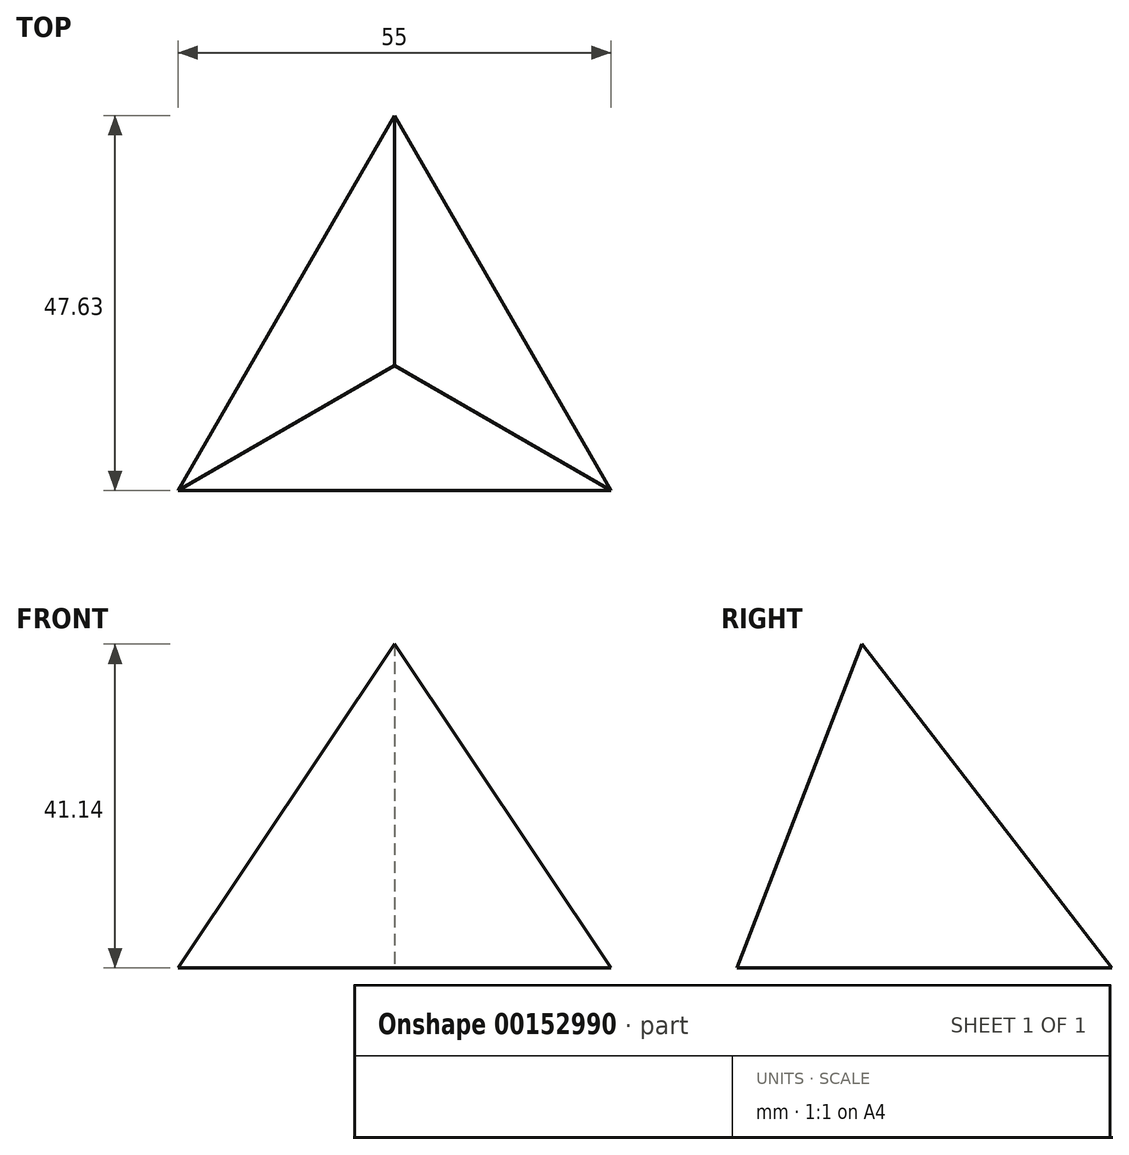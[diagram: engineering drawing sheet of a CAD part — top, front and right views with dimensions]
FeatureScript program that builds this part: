
annotation { "Feature Type Name" : "Feature", "Feature Type Description" : "" }
export const myFeature = defineFeature(function(context is Context, id is Id, definition is map)
    precondition{}
    {
        {
            var Q0;
            Q0=qCreatedBy(makeId("Top.planeOp"),FACE);
            var sketch = newSketch(context, id + "F0", { "sketchPlane" : qUnion([Q0])});
            skCircle(sketch, "E0.cCircle", {"center": v(0, 0) * mm, "radius": 31.75 * mm, "construction": true});
            skLineSegment(sketch, "E0.0", {"start": v(0, 31.75) * mm, "end": v(27.5, -15.87) * mm});
            skLineSegment(sketch, "E0.1", {"start": v(27.5, -15.87) * mm, "end": v(-27.5, -15.88) * mm});
            skLineSegment(sketch, "E0.2", {"start": v(-27.5, -15.88) * mm, "end": v(0, 31.75) * mm});
            skSolve(sketch);
        }
        {
            var Q0;
            Q0 = qSketchRegion(id + "F0", true);
            extrude(context, id + "F1", {"entities" : qUnion([Q0]), "depth" : 50.8 * mm, "hasDraft" : true, "draftAngle" : 21.1 * degree, "draftPullDirection" : true});
        }
    });
